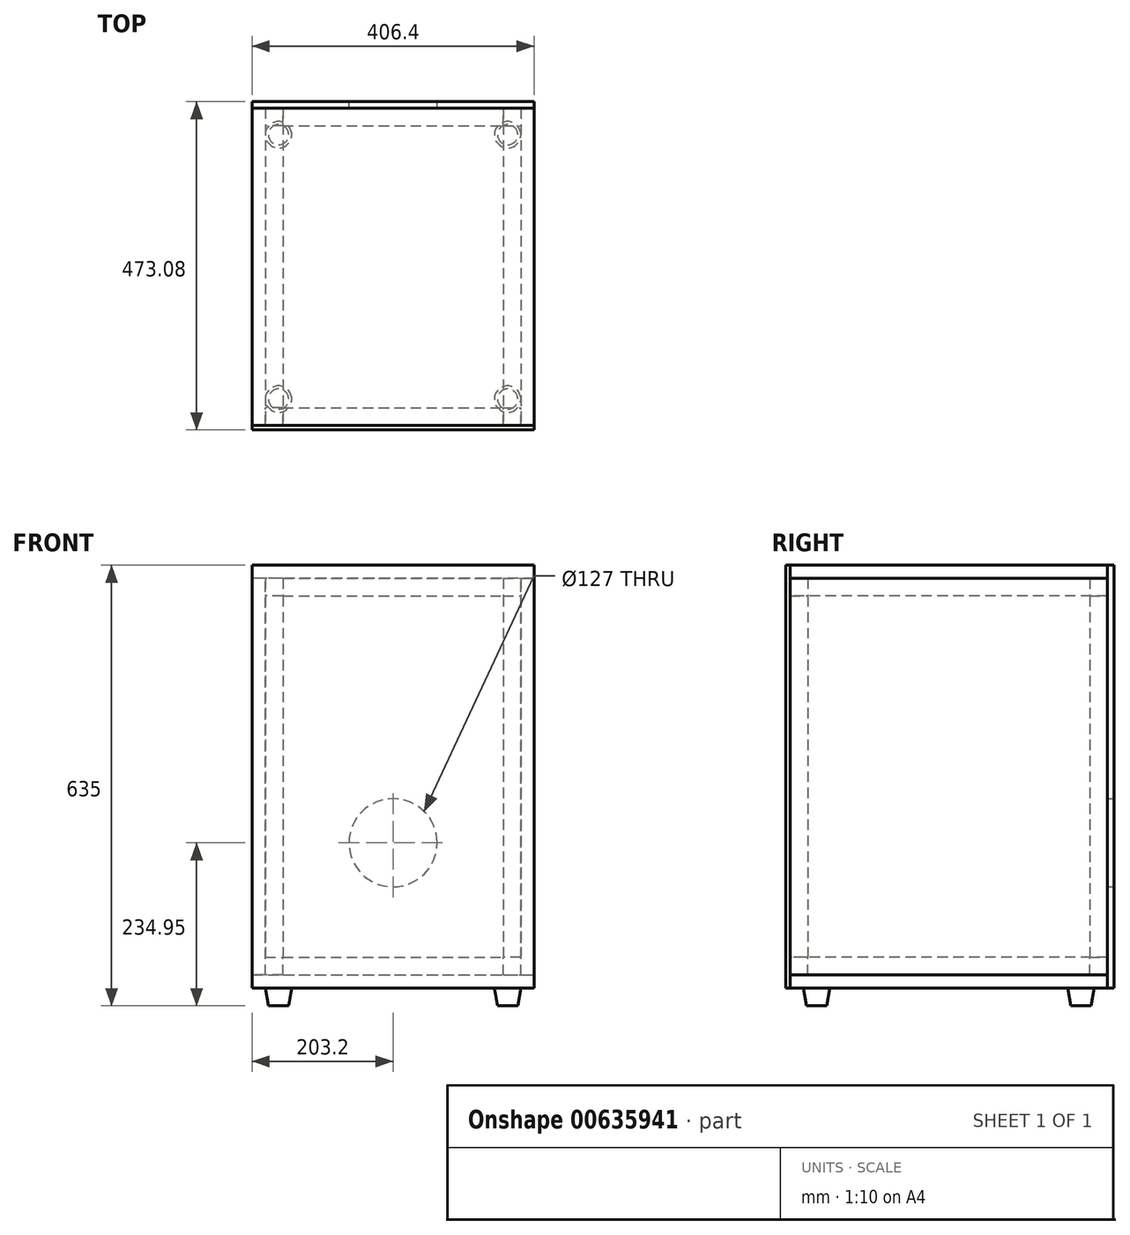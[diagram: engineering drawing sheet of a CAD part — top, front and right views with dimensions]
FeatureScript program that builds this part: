
annotation { "Feature Type Name" : "Feature", "Feature Type Description" : "" }
export const myFeature = defineFeature(function(context is Context, id is Id, definition is map)
    precondition{}
    {
        {
            var Q0;
            Q0=qCreatedBy(makeId("Top.planeOp"),FACE);
            var sketch = newSketch(context, id + "F0", { "sketchPlane" : qUnion([Q0])});
            skLineSegment(sketch, "E0.bottom", {"start": v(-203.2, -228.6) * mm, "end": v(203.2, -228.6) * mm});
            skLineSegment(sketch, "E0.top", {"start": v(-203.2, 228.6) * mm, "end": v(203.2, 228.6) * mm});
            skLineSegment(sketch, "E0.left", {"start": v(-203.2, -228.6) * mm, "end": v(-203.2, 228.6) * mm});
            skLineSegment(sketch, "E0.right", {"start": v(203.2, -228.6) * mm, "end": v(203.2, 228.6) * mm});
            skLineSegment(sketch, "E1", {"start": v(0, -228.6) * mm, "end": v(0, 228.6) * mm, "construction": true});
            skSolve(sketch);
        }
        {
            var Q0;
            Q0 = qSketchRegion(id + "F0", true);
            extrude(context, id + "F1", {"entities" : qUnion([Q0]), "depth" : 19.05 * mm, "offsetDistance" : 25.4 * mm});
        }
        {
            var Q0;
            Q0=makeQuery(id+"F1.opExtrude","CAP_FACE",FACE,{"disambiguationData":[OSD([sQuery(id+"F0.wireOp",EDGE,"E0.bottom"),sQuery(id+"F0.wireOp",EDGE,"E0.top"),sQuery(id+"F0.wireOp",EDGE,"E0.left"),sQuery(id+"F0.wireOp",EDGE,"E0.right")])],"isStart":true});
            cPlane(context, id + "F2", {"entities" : qUnion([Q0]), "cplaneType" : CPlaneType.OFFSET, "offset" : 609.6 * mm, "oppositeDirection" : true, "width" : 152.4 * mm, "height" : 152.4 * mm});
        }
        {
            var Q0;
            Q0=qCreatedBy(id+"F2.planeOp",FACE);
            var sketch = newSketch(context, id + "F3", { "sketchPlane" : qUnion([Q0])});
            skLineSegment(sketch, "E2.bottom", {"start": v(203.2, 228.6) * mm, "end": v(-203.2, 228.6) * mm});
            skLineSegment(sketch, "E2.top", {"start": v(203.2, -228.6) * mm, "end": v(-203.2, -228.6) * mm});
            skLineSegment(sketch, "E2.left", {"start": v(203.2, 228.6) * mm, "end": v(203.2, -228.6) * mm});
            skLineSegment(sketch, "E2.right", {"start": v(-203.2, 228.6) * mm, "end": v(-203.2, -228.6) * mm});
            skSolve(sketch);
        }
        {
            var Q0;
            Q0=makeQuery(id+"F3.imprint","IMPRINT",FACE,{"disambiguationData":[TD([[makeQuery(id+"F3.imprint","IMPRINT",EDGE,{"derivedFrom":sQuery(id+"F3.wireOp",EDGE,"E2.bottom")}),1.0]])]});
            extrude(context, id + "F4", {"entities" : qUnion([Q0]), "depth" : 19.05 * mm, "offsetDistance" : 25.4 * mm});
        }
        {
            var Q0;
            Q0=makeQuery(id+"F1.opExtrude","SWEPT_FACE",FACE,{"disambiguationData":[OSD([sQuery(id+"F0.wireOp",EDGE,"E0.right")])]});
            var sketch = newSketch(context, id + "F5", { "sketchPlane" : qUnion([Q0])});
            skLineSegment(sketch, "E3.bottom", {"start": v(-228.6, 19.05) * mm, "end": v(228.6, 19.05) * mm});
            skLineSegment(sketch, "E3.top", {"start": v(-228.6, 590.55) * mm, "end": v(228.6, 590.55) * mm});
            skLineSegment(sketch, "E3.left", {"start": v(-228.6, 19.05) * mm, "end": v(-228.6, 590.55) * mm});
            skLineSegment(sketch, "E3.right", {"start": v(228.6, 19.05) * mm, "end": v(228.6, 590.55) * mm});
            skSolve(sketch);
        }
        {
            var Q0;
            Q0=makeQuery(id+"F5.imprint","IMPRINT",FACE,{"disambiguationData":[TD([[makeQuery(id+"F5.imprint","IMPRINT",EDGE,{"derivedFrom":sQuery(id+"F5.wireOp",EDGE,"E3.bottom")}),1.0]])]});
            extrude(context, id + "F6", {"entities" : qUnion([Q0]), "oppositeDirection" : true, "depth" : 19.05 * mm, "offsetDistance" : 25.4 * mm});
        }
        {
            var Q0;
            Q0=makeQuery(id+"F6.opExtrude","SWEPT_BODY",BODY,{"disambiguationData":[OSD([sQuery(id+"F5.wireOp",EDGE,"E3.bottom"),sQuery(id+"F5.wireOp",EDGE,"E3.top"),sQuery(id+"F5.wireOp",EDGE,"E3.left"),sQuery(id+"F5.wireOp",EDGE,"E3.right")])]});
            var Q1;
            Q1=qCreatedBy(makeId("Right.planeOp"),FACE);
            mirror(context, id + "F7", {"entities" : qUnion([Q0]), "mirrorPlane" : qUnion([Q1])});
        }
        {
            var Q0;
            Q0=makeQuery(id+"F1.opExtrude","SWEPT_FACE",FACE,{"disambiguationData":[OSD([sQuery(id+"F0.wireOp",EDGE,"E0.bottom")])]});
            var sketch = newSketch(context, id + "F8", { "sketchPlane" : qUnion([Q0])});
            skLineSegment(sketch, "E4.bottom", {"start": v(203.2, 19.05) * mm, "end": v(158.75, 19.05) * mm});
            skLineSegment(sketch, "E4.top", {"start": v(184.15, 44.45) * mm, "end": v(158.75, 44.45) * mm});
            skLineSegment(sketch, "E4.left", {"start": v(184.15, 19.05) * mm, "end": v(184.15, 44.45) * mm});
            skLineSegment(sketch, "E4.right", {"start": v(158.75, 19.05) * mm, "end": v(158.75, 44.45) * mm});
            skSolve(sketch);
        }
        {
            var Q0;
            Q0=makeQuery(id+"F8.imprint","IMPRINT",FACE,{"disambiguationData":[TD([[makeQuery(id+"F8.imprint","IMPRINT",EDGE,{"derivedFrom":sQuery(id+"F8.wireOp",EDGE,"E4.bottom")}),1.0]])]});
            var Q1;
            Q1=makeQuery(id+"F1.opExtrude","SWEPT_FACE",FACE,{"disambiguationData":[OSD([sQuery(id+"F0.wireOp",EDGE,"E0.top")])]});
            extrude(context, id + "F9", {"entities" : qUnion([Q0]), "endBound" : BoundingType.UP_TO_SURFACE, "oppositeDirection" : true, "depth" : 38.1 * mm, "endBoundEntityFace" : qUnion([Q1]), "offsetDistance" : 25.4 * mm});
        }
        {
            var Q0;
            Q0=makeQuery(id+"F9.opExtrude","SWEPT_BODY",BODY,{"disambiguationData":[OSD([sQuery(id+"F8.wireOp",EDGE,"E4.bottom"),sQuery(id+"F8.wireOp",EDGE,"E4.top"),sQuery(id+"F8.wireOp",EDGE,"E4.left"),sQuery(id+"F8.wireOp",EDGE,"E4.right")])]});
            var Q1;
            Q1=qCreatedBy(makeId("Right.planeOp"),FACE);
            mirror(context, id + "F10", {"entities" : qUnion([Q0]), "mirrorPlane" : qUnion([Q1])});
        }
        {
            var Q0;
            Q0=makeQuery(id+"F9.opExtrude","SWEPT_FACE",FACE,{"disambiguationData":[OSD([sQuery(id+"F8.wireOp",EDGE,"E4.right")])]});
            var sketch = newSketch(context, id + "F11", { "sketchPlane" : qUnion([Q0])});
            skLineSegment(sketch, "E5.bottom", {"start": v(228.6, 19.05) * mm, "end": v(203.2, 19.05) * mm});
            skLineSegment(sketch, "E5.top", {"start": v(228.6, 44.45) * mm, "end": v(203.2, 44.45) * mm});
            skLineSegment(sketch, "E5.left", {"start": v(228.6, 19.05) * mm, "end": v(228.6, 44.45) * mm});
            skLineSegment(sketch, "E5.right", {"start": v(203.2, 19.05) * mm, "end": v(203.2, 44.45) * mm});
            skSolve(sketch);
        }
        {
            var Q0;
            Q0 = qSketchRegion(id + "F11", true);
            var Q1;
            Q1=makeQuery(id+"F10.opPattern","COPY",FACE,{"derivedFrom":makeQuery(id+"F9.opExtrude","SWEPT_FACE",FACE,{"disambiguationData":[OSD([sQuery(id+"F8.wireOp",EDGE,"E4.right")])]}),"instanceName":"1"});
            extrude(context, id + "F12", {"entities" : qUnion([Q0]), "endBound" : BoundingType.UP_TO_SURFACE, "depth" : 25.4 * mm, "endBoundEntityFace" : qUnion([Q1]), "offsetDistance" : 25.4 * mm});
        }
        {
            var Q0;
            Q0=makeQuery(id+"F12.opExtrude","SWEPT_BODY",BODY,{"disambiguationData":[OSD([sQuery(id+"F11.wireOp",EDGE,"E5.bottom"),sQuery(id+"F11.wireOp",EDGE,"E5.top"),sQuery(id+"F11.wireOp",EDGE,"E5.left"),sQuery(id+"F11.wireOp",EDGE,"E5.right")])]});
            var Q1;
            Q1=qCreatedBy(makeId("Front.planeOp"),FACE);
            mirror(context, id + "F13", {"entities" : qUnion([Q0]), "mirrorPlane" : qUnion([Q1])});
        }
        {
            var Q0;
            Q0=makeQuery(id+"F1.opExtrude","CAP_FACE",FACE,{"disambiguationData":[OSD([sQuery(id+"F0.wireOp",EDGE,"E0.bottom"),sQuery(id+"F0.wireOp",EDGE,"E0.top"),sQuery(id+"F0.wireOp",EDGE,"E0.left"),sQuery(id+"F0.wireOp",EDGE,"E0.right")])],"isStart":false});
            var Q1;
            Q1=makeQuery(id+"F4.opExtrude","CAP_FACE",FACE,{"disambiguationData":[OSD([sQuery(id+"F3.wireOp",EDGE,"E2.bottom"),sQuery(id+"F3.wireOp",EDGE,"E2.top"),sQuery(id+"F3.wireOp",EDGE,"E2.left"),sQuery(id+"F3.wireOp",EDGE,"E2.right")])],"isStart":false});
            cPlane(context, id + "F14", {"entities" : qUnion([Q0, Q1]), "cplaneType" : CPlaneType.MID_PLANE, "offset" : 25.4 * mm, "width" : 152.4 * mm, "height" : 152.4 * mm});
        }
        {
            var Q0;
            Q0=makeQuery(id+"F10.opPattern","COPY",BODY,{"derivedFrom":makeQuery(id+"F9.opExtrude","SWEPT_BODY",BODY,{"disambiguationData":[OSD([sQuery(id+"F8.wireOp",EDGE,"E4.bottom"),sQuery(id+"F8.wireOp",EDGE,"E4.top"),sQuery(id+"F8.wireOp",EDGE,"E4.left"),sQuery(id+"F8.wireOp",EDGE,"E4.right")])]}),"instanceName":"1"});
            var Q1;
            Q1=makeQuery(id+"F13.opPattern","COPY",BODY,{"derivedFrom":makeQuery(id+"F12.opExtrude","SWEPT_BODY",BODY,{"disambiguationData":[OSD([sQuery(id+"F11.wireOp",EDGE,"E5.bottom"),sQuery(id+"F11.wireOp",EDGE,"E5.top"),sQuery(id+"F11.wireOp",EDGE,"E5.left"),sQuery(id+"F11.wireOp",EDGE,"E5.right")])]}),"instanceName":"1"});
            var Q2;
            Q2=makeQuery(id+"F9.opExtrude","SWEPT_BODY",BODY,{"disambiguationData":[OSD([sQuery(id+"F8.wireOp",EDGE,"E4.bottom"),sQuery(id+"F8.wireOp",EDGE,"E4.top"),sQuery(id+"F8.wireOp",EDGE,"E4.left"),sQuery(id+"F8.wireOp",EDGE,"E4.right")])]});
            var Q3;
            Q3=makeQuery(id+"F12.opExtrude","SWEPT_BODY",BODY,{"disambiguationData":[OSD([sQuery(id+"F11.wireOp",EDGE,"E5.bottom"),sQuery(id+"F11.wireOp",EDGE,"E5.top"),sQuery(id+"F11.wireOp",EDGE,"E5.left"),sQuery(id+"F11.wireOp",EDGE,"E5.right")])]});
            var Q4;
            Q4=qCreatedBy(id+"F14.planeOp",FACE);
            mirror(context, id + "F15", {"entities" : qUnion([Q0, Q1, Q2, Q3]), "mirrorPlane" : qUnion([Q4])});
        }
        {
            var Q0;
            Q0=makeQuery(id+"F9.opExtrude","SWEPT_FACE",FACE,{"disambiguationData":[OSD([sQuery(id+"F8.wireOp",EDGE,"E4.top")])]});
            var sketch = newSketch(context, id + "F16", { "sketchPlane" : qUnion([Q0])});
            skLineSegment(sketch, "E6.bottom", {"start": v(184.15, -228.6) * mm, "end": v(158.75, -228.6) * mm});
            skLineSegment(sketch, "E6.top", {"start": v(184.15, -203.2) * mm, "end": v(158.75, -203.2) * mm});
            skLineSegment(sketch, "E6.left", {"start": v(184.15, -228.6) * mm, "end": v(184.15, -203.2) * mm});
            skLineSegment(sketch, "E6.right", {"start": v(158.75, -228.6) * mm, "end": v(158.75, -203.2) * mm});
            skSolve(sketch);
        }
        {
            var Q0;
            Q0 = qSketchRegion(id + "F16", true);
            var Q1;
            Q1=makeQuery(id+"F15.opPattern","COPY",FACE,{"derivedFrom":makeQuery(id+"F9.opExtrude","SWEPT_FACE",FACE,{"disambiguationData":[OSD([sQuery(id+"F8.wireOp",EDGE,"E4.top")])]}),"instanceName":"1"});
            extrude(context, id + "F17", {"entities" : qUnion([Q0]), "endBound" : BoundingType.UP_TO_SURFACE, "depth" : 25.4 * mm, "endBoundEntityFace" : qUnion([Q1]), "offsetDistance" : 25.4 * mm});
        }
        {
            var Q0;
            Q0=makeQuery(id+"F17.opExtrude","SWEPT_BODY",BODY,{"disambiguationData":[OSD([sQuery(id+"F16.wireOp",EDGE,"E6.bottom"),sQuery(id+"F16.wireOp",EDGE,"E6.top"),sQuery(id+"F16.wireOp",EDGE,"E6.left"),sQuery(id+"F16.wireOp",EDGE,"E6.right")])]});
            var Q1;
            Q1=qCreatedBy(makeId("Front.planeOp"),FACE);
            mirror(context, id + "F18", {"entities" : qUnion([Q0]), "mirrorPlane" : qUnion([Q1])});
        }
        {
            var Q0;
            Q0=makeQuery(id+"F17.opExtrude","SWEPT_BODY",BODY,{"disambiguationData":[OSD([sQuery(id+"F16.wireOp",EDGE,"E6.bottom"),sQuery(id+"F16.wireOp",EDGE,"E6.top"),sQuery(id+"F16.wireOp",EDGE,"E6.left"),sQuery(id+"F16.wireOp",EDGE,"E6.right")])]});
            var Q1;
            Q1=makeQuery(id+"F18.opPattern","COPY",BODY,{"derivedFrom":makeQuery(id+"F17.opExtrude","SWEPT_BODY",BODY,{"disambiguationData":[OSD([sQuery(id+"F16.wireOp",EDGE,"E6.bottom"),sQuery(id+"F16.wireOp",EDGE,"E6.top"),sQuery(id+"F16.wireOp",EDGE,"E6.left"),sQuery(id+"F16.wireOp",EDGE,"E6.right")])]}),"instanceName":"1"});
            var Q2;
            Q2=qCreatedBy(makeId("Right.planeOp"),FACE);
            mirror(context, id + "F19", {"entities" : qUnion([Q0, Q1]), "mirrorPlane" : qUnion([Q2])});
        }
        {
            var Q0;
            Q0=makeQuery(id+"F1.opExtrude","SWEPT_FACE",FACE,{"disambiguationData":[OSD([sQuery(id+"F0.wireOp",EDGE,"E0.top")])]});
            var sketch = newSketch(context, id + "F20", { "sketchPlane" : qUnion([Q0])});
            skLineSegment(sketch, "E7.bottom", {"start": v(-203.2, 0) * mm, "end": v(203.2, 0) * mm});
            skLineSegment(sketch, "E7.top", {"start": v(-203.2, 609.6) * mm, "end": v(203.2, 609.6) * mm});
            skLineSegment(sketch, "E7.left", {"start": v(-203.2, 0) * mm, "end": v(-203.2, 609.6) * mm});
            skLineSegment(sketch, "E7.right", {"start": v(203.2, 0) * mm, "end": v(203.2, 609.6) * mm});
            skSolve(sketch);
        }
        {
            var Q0;
            Q0 = qSketchRegion(id + "F20", true);
            extrude(context, id + "F21", {"entities" : qUnion([Q0]), "depth" : 9.52 * mm, "offsetDistance" : 25.4 * mm});
        }
        {
            var Q0;
            Q0=makeQuery(id+"F21.opExtrude","CAP_FACE",FACE,{"disambiguationData":[OSD([sQuery(id+"F20.wireOp",EDGE,"E7.bottom"),sQuery(id+"F20.wireOp",EDGE,"E7.top"),sQuery(id+"F20.wireOp",EDGE,"E7.left"),sQuery(id+"F20.wireOp",EDGE,"E7.right")])],"isStart":false});
            var sketch = newSketch(context, id + "F22", { "sketchPlane" : qUnion([Q0])});
            skCircle(sketch, "E8", {"center": v(0, 209.55) * mm, "radius": 63.5 * mm});
            skLineSegment(sketch, "E9", {"start": v(0, 19.05) * mm, "end": v(0, 209.55) * mm, "construction": true});
            skLineSegment(sketch, "E10", {"start": v(0, 209.55) * mm, "end": v(0, 400.05) * mm, "construction": true});
            skLineSegment(sketch, "E11", {"start": v(0, 400.05) * mm, "end": v(0, 590.55) * mm, "construction": true});
            skSolve(sketch);
        }
        {
            var Q0;
            Q0=makeQuery(id+"F22.imprint","IMPRINT",FACE,{"disambiguationData":[TD([[makeQuery(id+"F22.imprint","IMPRINT",EDGE,{"derivedFrom":sQuery(id+"F22.wireOp",EDGE,"E8")}),1.0]])]});
            extrude(context, id + "F23", {"entities" : qUnion([Q0]), "operationType" : NewBodyOperationType.REMOVE, "endBound" : BoundingType.UP_TO_NEXT, "oppositeDirection" : true, "depth" : 25.4 * mm, "offsetDistance" : 25.4 * mm});
        }
        {
            var Q0;
            Q0=makeQuery(id+"F1.opExtrude","SWEPT_FACE",FACE,{"disambiguationData":[OSD([sQuery(id+"F0.wireOp",EDGE,"E0.bottom")])]});
            var sketch = newSketch(context, id + "F24", { "sketchPlane" : qUnion([Q0])});
            skLineSegment(sketch, "E12.bottom", {"start": v(-203.2, 0) * mm, "end": v(203.2, 0) * mm});
            skLineSegment(sketch, "E12.top", {"start": v(-203.2, 609.6) * mm, "end": v(203.2, 609.6) * mm});
            skLineSegment(sketch, "E12.left", {"start": v(-203.2, 0) * mm, "end": v(-203.2, 609.6) * mm});
            skLineSegment(sketch, "E12.right", {"start": v(203.2, 0) * mm, "end": v(203.2, 609.6) * mm});
            skSolve(sketch);
        }
        {
            var Q0;
            {var subQ0=sQuery(id+"F24.wireOp",EDGE,"E12.top");Q0=makeQuery(id+"F24.imprint","IMPRINT",FACE,{"disambiguationData":[TD([[makeQuery(id+"F24.imprint","IMPRINT",EDGE,{"derivedFrom":subQ0}),-1.0]])]});}
            var Q1;
            {var subQ0=sQuery(id+"F24.wireOp",EDGE,"E12.bottom");Q1=makeQuery(id+"F24.imprint","IMPRINT",FACE,{"disambiguationData":[TD([[makeQuery(id+"F24.imprint","IMPRINT",EDGE,{"derivedFrom":subQ0}),1.0]])]});}
            extrude(context, id + "F25", {"entities" : qUnion([Q0, Q1]), "depth" : 6.35 * mm, "offsetDistance" : 25.4 * mm});
        }
        {
            var Q0;
            Q0=makeQuery(id+"F1.opExtrude","CAP_FACE",FACE,{"disambiguationData":[OSD([sQuery(id+"F0.wireOp",EDGE,"E0.bottom"),sQuery(id+"F0.wireOp",EDGE,"E0.top"),sQuery(id+"F0.wireOp",EDGE,"E0.left"),sQuery(id+"F0.wireOp",EDGE,"E0.right")])],"isStart":true});
            var sketch = newSketch(context, id + "F26", { "sketchPlane" : qUnion([Q0])});
            skLineSegment(sketch, "E13.bottom", {"start": v(203.2, 228.6) * mm, "end": v(165.1, 228.6) * mm, "construction": true});
            skLineSegment(sketch, "E13.top", {"start": v(203.2, 190.5) * mm, "end": v(165.1, 190.5) * mm, "construction": true});
            skLineSegment(sketch, "E13.left", {"start": v(203.2, 228.6) * mm, "end": v(203.2, 190.5) * mm, "construction": true});
            skLineSegment(sketch, "E13.right", {"start": v(165.1, 228.6) * mm, "end": v(165.1, 190.5) * mm, "construction": true});
            skCircle(sketch, "E14", {"center": v(165.1, 190.5) * mm, "radius": 19.05 * mm});
            skSolve(sketch);
        }
        {
            var Q0;
            Q0=makeQuery(id+"F26.imprint","IMPRINT",FACE,{"disambiguationData":[TD([[makeQuery(id+"F26.imprint","IMPRINT",EDGE,{"derivedFrom":sQuery(id+"F26.wireOp",EDGE,"E14")}),1.0]])]});
            extrude(context, id + "F27", {"entities" : qUnion([Q0]), "depth" : 25.4 * mm, "offsetDistance" : 25.4 * mm, "hasDraft" : true, "draftAngle" : 10 * degree, "draftPullDirection" : true});
        }
        {
            var Q0;
            Q0=makeQuery(id+"F27.opExtrude","SWEPT_BODY",BODY,{"disambiguationData":[OSD([sQuery(id+"F26.wireOp",EDGE,"E14")])]});
            var Q1;
            Q1=qCreatedBy(makeId("Front.planeOp"),FACE);
            mirror(context, id + "F28", {"entities" : qUnion([Q0]), "mirrorPlane" : qUnion([Q1])});
        }
        {
            var Q0;
            Q0=makeQuery(id+"F27.opExtrude","SWEPT_BODY",BODY,{"disambiguationData":[OSD([sQuery(id+"F26.wireOp",EDGE,"E14")])]});
            var Q1;
            Q1=makeQuery(id+"F28.opPattern","COPY",BODY,{"derivedFrom":makeQuery(id+"F27.opExtrude","SWEPT_BODY",BODY,{"disambiguationData":[OSD([sQuery(id+"F26.wireOp",EDGE,"E14")])]}),"instanceName":"1"});
            var Q2;
            Q2=qCreatedBy(makeId("Right.planeOp"),FACE);
            mirror(context, id + "F29", {"entities" : qUnion([Q0, Q1]), "mirrorPlane" : qUnion([Q2])});
        }
    });
